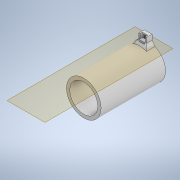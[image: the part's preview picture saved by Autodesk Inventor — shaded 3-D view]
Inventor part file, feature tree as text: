
AUTODESK INVENTOR PART (.ipt)
format: ipt  version: 2021 (Build 250183000, 183)  size: 533,504 bytes
history: native  units: in
note: dims shown in document units (in); Inventor stores cm internally (conversion verified against a paired STEP export)
features: projected_geometry x10, extrude x8, sketch x6, fillet x2, plane x1, chamfer x1
ambient origin geometry x8: Origin, YZ Plane, XZ Plane, XY Plane, X Axis, Y Axis, Z Axis, Center Point
bodies: Solid1 (feature_tree)
feature tree (28):
  extrude  "Extrusion1"  Depth=3.2677in TaperAngle=0.0deg
  plane  "Work Plane1"
  extrude  "Extrusion7"  Depth=3.189in TaperAngle=0.0deg
  extrude  "Extrusion8"  Depth=0.3937in
  extrude  "Extrusion9"  Depth=0.3937in
  extrude  "Extrusion10"  Depth=0.0295in TaperAngle=0.0deg
  extrude  "Extrusion11"  Depth=0.3937in
  extrude  "Extrusion13"  Depth=0.3937in TaperAngle=0.0deg
  chamfer  "Chamfer4"  Distance=1.1811in
  extrude  "Extrusion14"  Depth=0.3937in
  fillet  "Fillet11"  Radius=0.3937in
  fillet  "Fillet12"  Radius=0.0059in
  sketch  "Sketch2"  dims[d2=1.752in d3=3.2677in d4=0.0in]
  sketch  "Sketch9"  dims[d54=1.4173in d55=3.189in d56=0.0in]
  projected_geometry  "Projected Loop7"
  sketch  "Sketch10"  dims[d57=0.3937in d58=0.2756in]
  projected_geometry  "Projected Loop8"
  sketch  "Sketch11"  dims[d59=0.3937in d60=0.0236in d61=0.0in d62=0.0in d63=0.1693in]
  projected_geometry  "Projected Loop9"
  projected_geometry  "Projected Loop10"
  projected_geometry  "Projected Loop11"
  projected_geometry  "Projected Loop12"
  projected_geometry  "Projected Loop14"
  sketch  "Sketch16"  dims[d64=0.1024in d66=0.0295in d67=0.0in]
  projected_geometry  "Projected Loop16"
  sketch  "Sketch17"  dims[d68=0.0591in d69=0.0591in d71=0.1969in d72=0.0in d76=1.1811in d77=0.0in d92=0.1181in d93=0.3937in d94=0.0in d96=0.0059in d103=0.1575in d104=0.0787in d105=45.0deg d109=0.2756in d110=0.0787in d111=0.0in d116=0.4724in d117=0.3937in d121=0.0984in d19=0.0197in d20=0.0344in d21=0.0197in d22=0.0344in]
  projected_geometry  "Projected Loop17"
  projected_geometry  "Projected Loop18"
